# Revit family: LM0326351_Mueble Plus Vessel 70 cm CoronaStone Izquierdo
name_source: partatom
category: Plumbing Fixtures
units: mm (PartAtom-declared; Revit-internal decimal feet)

## family parameters
Always vertical = Yes
Cut with Voids When Loaded = No
Host = Wall
OmniClass Number = 23.45.05.14.14
OmniClass Title = Sinks/Lavatories
Part Type = Normal
Room Calculation Point = No
Round Connector Dimension = Use Diameter
Shared = No

## types (1)
- Type 1
    Alto = 435 mm
    Ancho = 696 mm  [stored 2.28346 ft]
    Creado por = IDD
    Densidad = 15mm 670 kg./m^3.
    Dimensiones generales producto (H * W * D) = 17,13” x 27,56” x 17,72” (435,0 x 700 x 450 mm)
    Fabricante = Corona
    Fecha de creación = 29/07/2020
    Garantía = 5 años
    Material = Corona_Madera_Aglomerada_Gales
    Peso Bruto aprox = 24 lb (10,9 kg)
    Peso Neto aprox = 13,4 lb (12,6 kg)
    Profundidad = 448 mm  [stored 1.46982 ft]
    Referencia = LM0326351
    Resistencia a la humedad = 8%
    URL = https://corona.co

note: [stored X ft] marks values corroborated as IEEE doubles in the binary element streams (Revit-internal decimal feet)

## geometry (parser evidence)
native form markers: Sweep x5
no freeform markers — native parametric forms only
